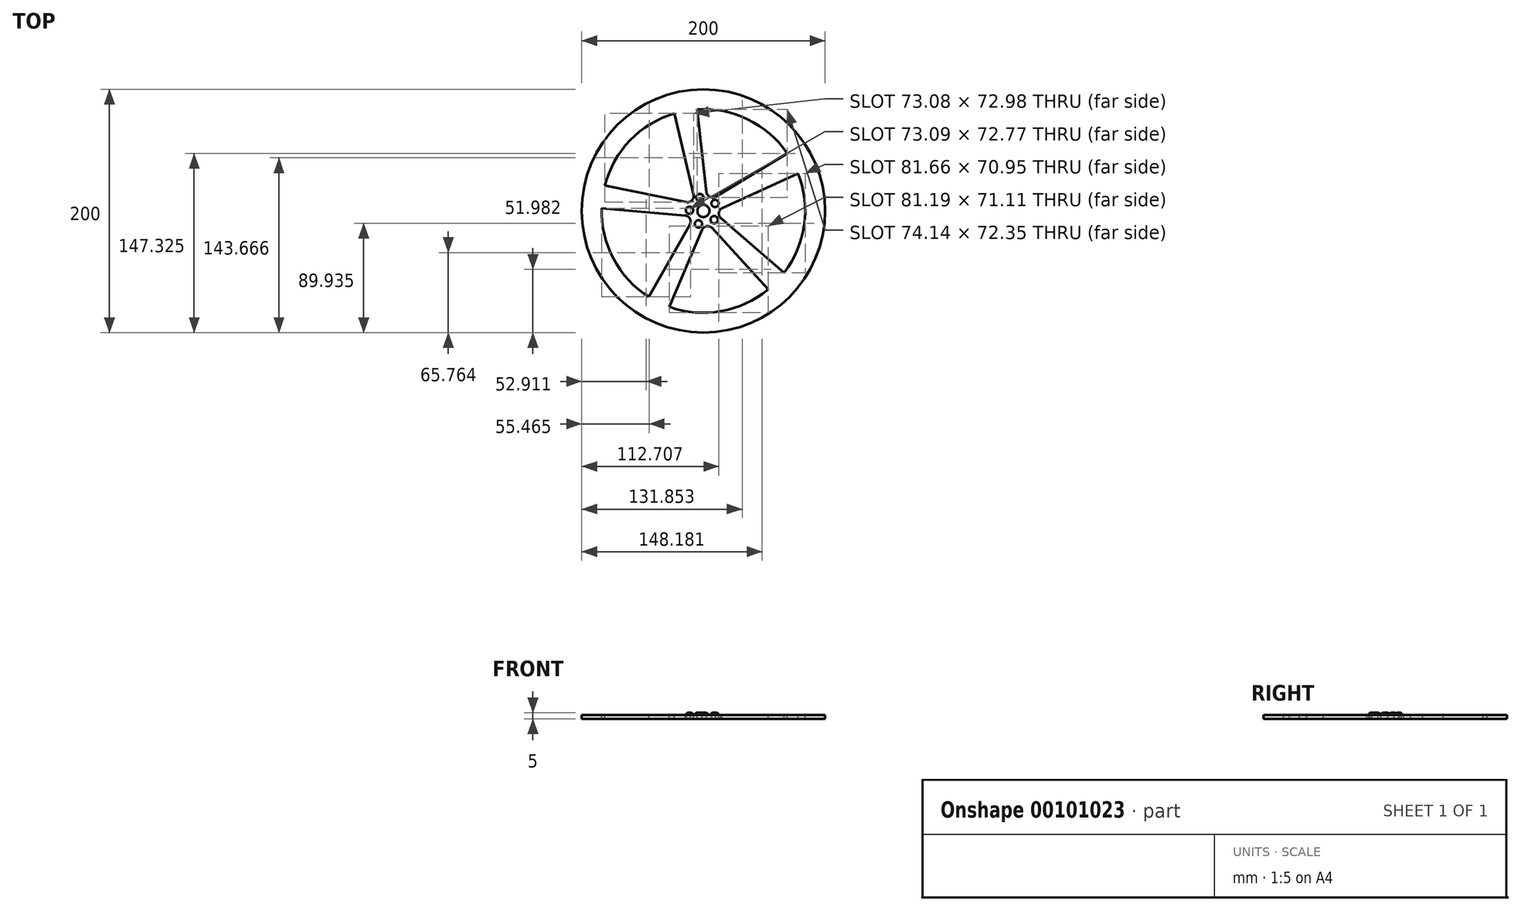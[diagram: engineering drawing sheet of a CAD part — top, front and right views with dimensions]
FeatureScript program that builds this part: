
annotation { "Feature Type Name" : "Feature", "Feature Type Description" : "" }
export const myFeature = defineFeature(function(context is Context, id is Id, definition is map)
    precondition{}
    {
        {
            var Q0;
            Q0=qCreatedBy(makeId("Top.planeOp"),FACE);
            var sketch = newSketch(context, id + "F0", { "sketchPlane" : qUnion([Q0])});
            skCircle(sketch, "E0", {"center": v(0, 0) * mm, "radius": 100 * mm});
            skSolve(sketch);
        }
        {
            var Q0;
            Q0 = qSketchRegion(id + "F0", true);
            extrude(context, id + "F1", {"entities" : qUnion([Q0]), "depth" : 3 * mm});
        }
        {
            var Q0;
            Q0=makeQuery(id+"F1.opExtrude","CAP_FACE",FACE,{"disambiguationData":[OSD([sQuery(id+"F0.wireOp",EDGE,"E0")])],"isStart":false});
            var sketch = newSketch(context, id + "F2", { "sketchPlane" : qUnion([Q0])});
            skCircle(sketch, "E1.cCircle", {"center": v(0, 0) * mm, "radius": 9.24 * mm, "construction": true});
            skCircle(sketch, "E2", {"center": v(-2.96, 11.03) * mm, "radius": 3 * mm});
            skCircle(sketch, "E3", {"center": v(9.58, 6.23) * mm, "radius": 3 * mm});
            skCircle(sketch, "E4", {"center": v(-11.4, 0.6) * mm, "radius": 3 * mm});
            skCircle(sketch, "E5", {"center": v(-4.09, -10.67) * mm, "radius": 3 * mm});
            skCircle(sketch, "E6", {"center": v(8.88, -7.19) * mm, "radius": 3 * mm});
            skSolve(sketch);
        }
        {
            var Q0;
            Q0 = qSketchRegion(id + "F2", true);
            extrude(context, id + "F3", {"entities" : qUnion([Q0]), "operationType" : NewBodyOperationType.ADD, "depth" : 2 * mm});
        }
        {
            var Q0;
            Q0=makeQuery(id+"F1.opExtrude","CAP_FACE",FACE,{"disambiguationData":[OSD([sQuery(id+"F0.wireOp",EDGE,"E0")])],"isStart":false});
            var sketch = newSketch(context, id + "F4", { "sketchPlane" : qUnion([Q0])});
            skCircle(sketch, "E7", {"center": v(0, 0) * mm, "radius": 88.24 * mm});
            skCircle(sketch, "E8", {"center": v(0, 0) * mm, "radius": 5 * mm});
            skSolve(sketch);
        }
        {
            var Q0;
            Q0=makeQuery(id+"F4.imprint","IMPRINT",FACE,{"disambiguationData":[TD([[makeQuery(id+"F4.imprint","IMPRINT",EDGE,{"derivedFrom":sQuery(id+"F4.wireOp",EDGE,"E8")}),1.0]])]});
            extrude(context, id + "F5", {"entities" : qUnion([Q0]), "operationType" : NewBodyOperationType.ADD, "depth" : 2 * mm});
        }
        {
            var Q0;
            Q0=makeQuery(id+"F3.opExtrude","CAP_EDGE",EDGE,{"disambiguationData":[OSD([sQuery(id+"F2.wireOp",EDGE,"E2")])],"isStart":false});
            var Q1;
            Q1=makeQuery(id+"F3.opExtrude","CAP_EDGE",EDGE,{"disambiguationData":[OSD([sQuery(id+"F2.wireOp",EDGE,"E3")])],"isStart":false});
            var Q2;
            Q2=makeQuery(id+"F3.opExtrude","CAP_EDGE",EDGE,{"disambiguationData":[OSD([sQuery(id+"F2.wireOp",EDGE,"E4")])],"isStart":false});
            var Q3;
            Q3=makeQuery(id+"F3.opExtrude","CAP_EDGE",EDGE,{"disambiguationData":[OSD([sQuery(id+"F2.wireOp",EDGE,"E5")])],"isStart":false});
            var Q4;
            Q4=makeQuery(id+"F3.opExtrude","CAP_EDGE",EDGE,{"disambiguationData":[OSD([sQuery(id+"F2.wireOp",EDGE,"E6")])],"isStart":false});
            fillet(context, id + "F6", {"entities" : qUnion([Q0, Q1, Q2, Q3, Q4]), "radius" : 2 * mm, "tangentPropagation" : true, "allowEdgeOverflow" : false});
        }
        {
            var Q0;
            Q0=makeQuery(id+"F5.opExtrude","CAP_FACE",FACE,{"disambiguationData":[OSD([sQuery(id+"F4.wireOp",EDGE,"E8")])],"isStart":false});
            fillet(context, id + "F7", {"entities" : qUnion([Q0]), "radius" : 5 * mm, "tangentPropagation" : true, "allowEdgeOverflow" : false});
        }
        {
            var Q0;
            Q0=makeQuery(id+"F1.opExtrude","CAP_FACE",FACE,{"disambiguationData":[OSD([sQuery(id+"F0.wireOp",EDGE,"E0")])],"isStart":false});
            var sketch = newSketch(context, id + "F8", { "sketchPlane" : qUnion([Q0])});
            skCircle(sketch, "E9", {"center": v(0, 0) * mm, "radius": 83.66 * mm});
            skCircle(sketch, "E10.cCircle", {"center": v(0, 0) * mm, "radius": 14.42 * mm, "construction": true});
            skLineSegment(sketch, "E10.0", {"start": v(-15.57, -8.69) * mm, "end": v(-13.07, 12.12) * mm});
            skLineSegment(sketch, "E10.1", {"start": v(-13.07, 12.12) * mm, "end": v(7.5, 16.18) * mm});
            skLineSegment(sketch, "E10.2", {"start": v(7.5, 16.18) * mm, "end": v(17.7, -2.13) * mm});
            skLineSegment(sketch, "E10.3", {"start": v(17.7, -2.13) * mm, "end": v(3.45, -17.5) * mm});
            skLineSegment(sketch, "E10.4", {"start": v(3.45, -17.5) * mm, "end": v(-15.57, -8.69) * mm});
            skPoint(sketch, "E10.0.midPoint", {"position": v(-14.32, 1.72) * mm});
            skArc(sketch, "E11", {"start": v(-13.67, 7.13) * mm, "mid": v(-9.38, 8.7) * mm, "end": v(-8.14, 13.1) * mm});
            skCircle(sketch, "E12.cCircle", {"center": v(0, 0) * mm, "radius": 83.66 * mm, "construction": true});
            skArc(sketch, "E13", {"start": v(-81.02, 20.84) * mm, "mid": v(-29.54, 28.47) * mm, "end": v(-23.8, 80.2) * mm});
            skLineSegment(sketch, "E14", {"start": v(-8.14, 13.1) * mm, "end": v(-23.8, 80.2) * mm});
            skLineSegment(sketch, "E15", {"start": v(-13.67, 7.13) * mm, "end": v(-81.02, 20.84) * mm});
            skLineSegment(sketch, "E16.1.0", {"start": v(-11, -10.8) * mm, "end": v(-44.86, -70.62) * mm});
            skLineSegment(sketch, "E16.1.1", {"start": v(-14.97, -3.69) * mm, "end": v(-83.63, 2.15) * mm});
            skArc(sketch, "E16.1.2", {"start": v(-11, -10.8) * mm, "mid": v(-11.18, -6.23) * mm, "end": v(-14.97, -3.69) * mm});
            skLineSegment(sketch, "E16.2.0", {"start": v(6.87, -13.8) * mm, "end": v(53.3, -64.49) * mm});
            skLineSegment(sketch, "E16.2.1", {"start": v(-1.12, -15.38) * mm, "end": v(-27.89, -78.88) * mm});
            skArc(sketch, "E16.2.2", {"start": v(6.87, -13.8) * mm, "mid": v(2.48, -12.56) * mm, "end": v(-1.12, -15.38) * mm});
            skLineSegment(sketch, "E16.3.0", {"start": v(15.25, 2.27) * mm, "end": v(77.8, 30.77) * mm});
            skLineSegment(sketch, "E16.3.1", {"start": v(14.28, -5.81) * mm, "end": v(66.4, -50.9) * mm});
            skArc(sketch, "E16.3.2", {"start": v(15.25, 2.27) * mm, "mid": v(12.7, -1.53) * mm, "end": v(14.28, -5.81) * mm});
            skLineSegment(sketch, "E16.4.0", {"start": v(2.56, 15.2) * mm, "end": v(-5.22, 83.5) * mm});
            skLineSegment(sketch, "E16.4.1", {"start": v(9.94, 11.78) * mm, "end": v(68.92, 47.42) * mm});
            skArc(sketch, "E16.4.2", {"start": v(2.56, 15.2) * mm, "mid": v(5.38, 11.61) * mm, "end": v(9.94, 11.78) * mm});
            skSolve(sketch);
        }
        {
            var Q0;
            {var subQ0=sQuery(id+"F8.wireOp",EDGE,"E16.4.0");Q0=makeQuery(id+"F8.imprint","IMPRINT",FACE,{"disambiguationData":[TD([[makeQuery(id+"F8.imprint","IMPRINT",EDGE,{"derivedFrom":subQ0}),-1.0]])]});}
            var Q1;
            {var subQ0=sQuery(id+"F8.wireOp",EDGE,"E15");var subQ1=sQuery(id+"F8.wireOp",EDGE,"E13");var subQ6=makeQuery(id+"F8.imprint","INTERSECT",VERTEX,{"derivedFrom":[subQ1,subQ0]});Q1=makeQuery(id+"F8.imprint","IMPRINT",FACE,{"disambiguationData":[TD([[makeQuery(id+"F8.imprint","IMPRINT",EDGE,{"disambiguationData":[TD([[subQ6,-1.0]])],"derivedFrom":subQ1}),1.0]])]});}
            var Q2;
            {var subQ0=sQuery(id+"F8.wireOp",EDGE,"E16.1.0");Q2=makeQuery(id+"F8.imprint","IMPRINT",FACE,{"disambiguationData":[TD([[makeQuery(id+"F8.imprint","IMPRINT",EDGE,{"derivedFrom":subQ0}),-1.0]])]});}
            var Q3;
            {var subQ0=sQuery(id+"F8.wireOp",EDGE,"E16.2.0");Q3=makeQuery(id+"F8.imprint","IMPRINT",FACE,{"disambiguationData":[TD([[makeQuery(id+"F8.imprint","IMPRINT",EDGE,{"derivedFrom":subQ0}),-1.0]])]});}
            var Q4;
            {var subQ0=sQuery(id+"F8.wireOp",EDGE,"E16.3.0");Q4=makeQuery(id+"F8.imprint","IMPRINT",FACE,{"disambiguationData":[TD([[makeQuery(id+"F8.imprint","IMPRINT",EDGE,{"derivedFrom":subQ0}),-1.0]])]});}
            var Q5;
            {var subQ4=sQuery(id+"F8.wireOp",EDGE,"E13");var subQ6=sQuery(id+"F8.wireOp",EDGE,"E15");var subQ7=makeQuery(id+"F8.imprint","INTERSECT",VERTEX,{"derivedFrom":[subQ4,subQ6]});Q5=makeQuery(id+"F8.imprint","IMPRINT",FACE,{"disambiguationData":[TD([[makeQuery(id+"F8.imprint","IMPRINT",EDGE,{"disambiguationData":[TD([[subQ7,-1.0]])],"derivedFrom":subQ4}),-1.0]])]});}
            var Q6;
            {var subQ3=sQuery(id+"F8.wireOp",EDGE,"E16.4.2");Q6=makeQuery(id+"F8.imprint","IMPRINT",FACE,{"disambiguationData":[TD([[makeQuery(id+"F8.imprint","IMPRINT",EDGE,{"derivedFrom":subQ3}),1.0]])]});}
            var Q7;
            {var subQ3=sQuery(id+"F8.wireOp",EDGE,"E11");Q7=makeQuery(id+"F8.imprint","IMPRINT",FACE,{"disambiguationData":[TD([[makeQuery(id+"F8.imprint","IMPRINT",EDGE,{"derivedFrom":subQ3}),1.0]])]});}
            var Q8;
            {var subQ3=sQuery(id+"F8.wireOp",EDGE,"E16.1.2");Q8=makeQuery(id+"F8.imprint","IMPRINT",FACE,{"disambiguationData":[TD([[makeQuery(id+"F8.imprint","IMPRINT",EDGE,{"derivedFrom":subQ3}),1.0]])]});}
            var Q9;
            {var subQ3=sQuery(id+"F8.wireOp",EDGE,"E16.2.2");Q9=makeQuery(id+"F8.imprint","IMPRINT",FACE,{"disambiguationData":[TD([[makeQuery(id+"F8.imprint","IMPRINT",EDGE,{"derivedFrom":subQ3}),1.0]])]});}
            var Q10;
            {var subQ3=sQuery(id+"F8.wireOp",EDGE,"E16.3.2");Q10=makeQuery(id+"F8.imprint","IMPRINT",FACE,{"disambiguationData":[TD([[makeQuery(id+"F8.imprint","IMPRINT",EDGE,{"derivedFrom":subQ3}),1.0]])]});}
            extrude(context, id + "F9", {"entities" : qUnion([Q0, Q1, Q2, Q3, Q4, Q5, Q6, Q7, Q8, Q9, Q10]), "operationType" : NewBodyOperationType.REMOVE, "endBound" : BoundingType.UP_TO_NEXT, "oppositeDirection" : true, "depth" : 25 * mm});
        }
    });
